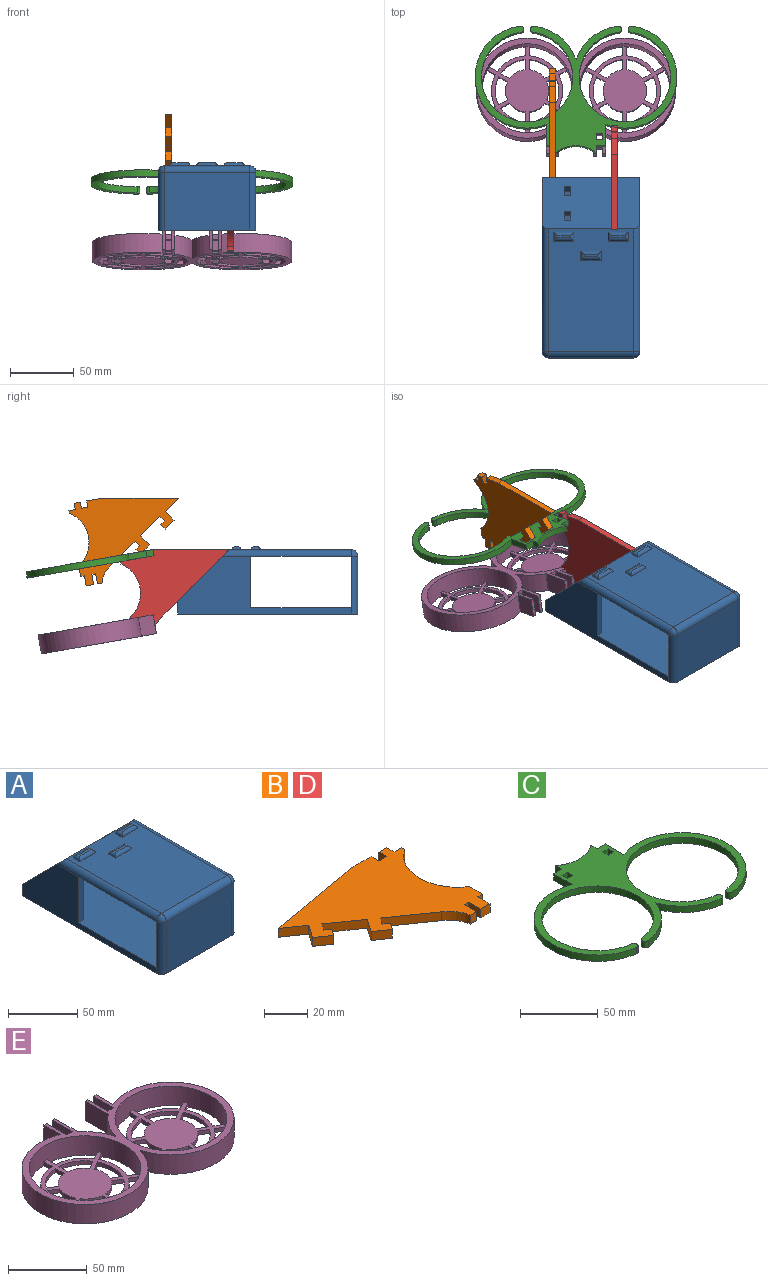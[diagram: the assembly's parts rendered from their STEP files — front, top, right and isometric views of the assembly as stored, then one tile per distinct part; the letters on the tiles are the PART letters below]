
ASSEMBLY  parts=5 mates=10
PART A: 54 faces, bbox 77x142x53 mm
  f0: plane 67x37.57mm, normal (0,-0.71,-0.71), area 3359.9mm2, adj f1,f5,f12,f13,f14,f15,f16,f17
  f1: plane 67x2.93mm, normal (0,-1,0), area 196.2mm2, adj f0,f2,f51,f53
  f2: plane 132x77mm, normal (0,0,1), area 9638.3mm2, adj f1,f4,f10,f11,f50,f51,f52,f53
  f3: plane 96.5x67mm, normal (0,0,1), area 6129.5mm2, adj f7,f31,f32,f33,f34,f35,f36,f37
  f4: plane 77x40.5mm, normal (0,1,0), area 3118.5mm2, adj f2,f5,f43,f46
  f5: plane 94.43x77mm, normal (0,0,-1), area 7121mm2, adj f0,f4,f44,f45,f50,f51,f52,f53
  f6: plane 77x10mm, normal (0,1,0), area 770mm2, adj f7,f9,f10,f11
  f7: plane 77x40.5mm, normal (0,0.71,0.71), area 4195.1mm2, adj f3,f6,f10,f11,f12,f13,f14,f15
  f8: plane 67x45.5mm, normal (0,-1,0), area 3048.5mm2, adj f9,f43,f46,f49
  f9: plane 142x77mm, normal (0,0,-1), area 10923.3mm2, adj f6,f8,f10,f11,f43,f46
  f10: plane 137x45.5mm, normal (1,0,0), area 2386.5mm2, adj f2,f6,f7,f9,f45,f46,f50
  f11: plane 137x45.5mm, normal (-1,0,0), area 2386.5mm2, adj f2,f6,f7,f9,f43,f44,f52
  f12: plane 5x3.54mm, normal (0,-0.71,0.71), area 25mm2, adj f0,f7,f13,f15
  f13: plane 10.61x10.61mm, normal (1,0,0), area 50mm2, adj f0,f7,f12,f14
  f14: plane 5x3.54mm, normal (0,0.71,-0.71), area 25mm2, adj f0,f7,f13,f15
  f15: plane 10.61x10.61mm, normal (-1,0,0), area 50mm2, adj f0,f7,f12,f14
  f16: plane 10.61x10.61mm, normal (1,0,0), area 50mm2, adj f0,f7,f17,f19
  f17: plane 5x3.54mm, normal (0,0.71,-0.71), area 25mm2, adj f0,f7,f16,f18
  f18: plane 10.61x10.61mm, normal (-1,0,0), area 50mm2, adj f0,f7,f17,f19
  f19: plane 5x3.54mm, normal (0,-0.71,0.71), area 25mm2, adj f0,f7,f16,f18
  f20: plane 10.61x10.61mm, normal (1,0,0), area 50mm2, adj f0,f7,f21,f23
  f21: plane 5x3.54mm, normal (0,0.71,-0.71), area 25mm2, adj f0,f7,f20,f22
  f22: plane 10.61x10.61mm, normal (-1,0,0), area 50mm2, adj f0,f7,f21,f23
  f23: plane 5x3.54mm, normal (0,-0.71,0.71), area 25mm2, adj f0,f7,f20,f22
  f24: plane 5x3.54mm, normal (0,-0.71,0.71), area 25mm2, adj f0,f7,f25,f27
  f25: plane 10.61x10.61mm, normal (1,0,0), area 50mm2, adj f0,f7,f24,f26
  f26: plane 5x3.54mm, normal (0,0.71,-0.71), area 25mm2, adj f0,f7,f25,f27
  f27: plane 10.61x10.61mm, normal (-1,0,0), area 50mm2, adj f0,f7,f24,f26
  f28: plane 11x2mm, normal (0,0,1), area 22mm2, adj f39,f40,f41,f42
  f29: plane 11x2mm, normal (0,0,1), area 22mm2, adj f31,f32,f33,f34
  f30: plane 11x2mm, normal (0,0,1), area 22mm2, adj f35,f36,f37,f38
  f31: cylinder r=2.5mm len=7mm, axis (0,-1,0), area 20.4mm2, adj f3,f29,f32,f33
  f32: cylinder r=2.5mm len=16mm, axis (-1,0,0), area 55.7mm2, adj f3,f29,f31,f34
  f33: cylinder r=2.5mm len=16mm, axis (1,0,0), area 55.7mm2, adj f3,f29,f31,f34
  f34: cylinder r=2.5mm len=7mm, axis (0,1,0), area 20.4mm2, adj f3,f29,f32,f33
  f35: cylinder r=2.5mm len=7mm, axis (0,-1,0), area 20.4mm2, adj f3,f30,f36,f37
  f36: cylinder r=2.5mm len=16mm, axis (-1,0,0), area 55.7mm2, adj f3,f30,f35,f38
  f37: cylinder r=2.5mm len=16mm, axis (1,0,0), area 55.7mm2, adj f3,f30,f35,f38
  f38: cylinder r=2.5mm len=7mm, axis (0,1,0), area 20.4mm2, adj f3,f30,f36,f37
  f39: cylinder r=2.5mm len=7mm, axis (0,-1,0), area 20.4mm2, adj f3,f28,f40,f41
  f40: cylinder r=2.5mm len=16mm, axis (-1,0,0), area 55.7mm2, adj f3,f28,f39,f42
  f41: cylinder r=2.5mm len=16mm, axis (1,0,0), area 55.7mm2, adj f3,f28,f39,f42
  f42: cylinder r=2.5mm len=7mm, axis (0,1,0), area 20.4mm2, adj f3,f28,f40,f41
  f43: cylinder r=5mm len=45.5mm, axis (0,0,1), area 357.4mm2, adj f4,f8,f9,f11,f47
  f44: cylinder r=5mm len=101.5mm, axis (0,1,0), area 772.2mm2, adj f3,f5,f7,f11,f47
  f45: cylinder r=5mm len=101.5mm, axis (0,-1,0), area 772.2mm2, adj f3,f5,f7,f10,f48
  f46: cylinder r=5mm len=45.5mm, axis (0,0,-1), area 357.4mm2, adj f4,f8,f9,f10,f48
  f47: sphere r=5mm, area 39.3mm2, adj f43,f44,f49
  f48: sphere r=5mm, area 39.3mm2, adj f45,f46,f49
  f49: cylinder r=5mm len=67mm, axis (1,0,0), area 526.2mm2, adj f3,f8,f47,f48
  f50: plane 40.5x5mm, normal (0,-1,0), area 202.5mm2, adj f2,f5,f10,f51
  f51: plane 52.57x40.5mm, normal (-1,0,0), area 1423.3mm2, adj f0,f1,f2,f5,f50
  f52: plane 40.5x5mm, normal (0,-1,0), area 202.5mm2, adj f2,f5,f11,f53
  f53: plane 52.57x40.5mm, normal (1,0,0), area 1423.3mm2, adj f0,f1,f2,f5,f52
PART B: 35 faces, bbox 86.3x65.7x5 mm
  f0: plane 5x5mm, normal (1,0,0), area 25mm2, adj f1,f32,f33,f34
  f1: plane 13x5mm, normal (0,1,0), area 65mm2, adj f0,f2,f33,f34
  f2: plane 58.34x10.29mm, normal (-0.17,0.98,0), area 296.2mm2, adj f1,f3,f33,f34
  f3: plane 11.88x8.32mm, normal (-0.57,-0.82,0), area 72.5mm2, adj f2,f4,f33,f34
  f4: plane 8.19x5.74mm, normal (-0.82,0.57,0), area 50mm2, adj f3,f5,f33,f34
  f5: plane 8.19x5.74mm, normal (-0.57,-0.82,0), area 50mm2, adj f4,f6,f33,f34
  f6: plane 5x4.15mm, normal (0.82,-0.57,0), area 25.2mm2, adj f5,f7,f33,f34
  f7: plane 5x3.3mm, normal (0.56,0.83,0), area 20mm2, adj f6,f8,f33,f34
  f8: plane 5x4.1mm, normal (0.82,-0.57,0), area 25mm2, adj f7,f9,f33,f34
  f9: plane 17.64x12.35mm, normal (-0.57,-0.82,0), area 107.7mm2, adj f8,f10,f33,f34
  f10: plane 8.19x5.74mm, normal (-0.82,0.57,0), area 50mm2, adj f9,f11,f33,f34
  f11: plane 8.19x5.74mm, normal (-0.57,-0.82,0), area 50mm2, adj f10,f12,f33,f34
  f12: plane 5x4.1mm, normal (0.82,-0.57,0), area 25mm2, adj f11,f13,f33,f34
  f13: plane 5x3.28mm, normal (0.57,0.82,0), area 20mm2, adj f12,f14,f33,f34
  f14: plane 5x4.1mm, normal (0.82,-0.57,0), area 25mm2, adj f13,f15,f33,f34
  f15: plane 23.48x16.44mm, normal (-0.57,-0.82,0), area 143.3mm2, adj f14,f16,f33,f34
  f16: cylinder r=20mm len=8.98mm, axis (0,0,1), area 58.1mm2, adj f15,f17,f33,f34
  f17: plane 5x2.46mm, normal (-0.98,-0.17,0), area 12.5mm2, adj f16,f18,f33,f34
  f18: plane 5x4mm, normal (0,-1,0), area 20mm2, adj f17,f19,f33,f34
  f19: plane 8x5mm, normal (1,0,0), area 40mm2, adj f18,f20,f33,f34
  f20: plane 5x3mm, normal (0,-1,0), area 15mm2, adj f19,f21,f33,f34
  f21: plane 8x5mm, normal (-1,0,0), area 40mm2, adj f20,f22,f33,f34
  f22: plane 6x5mm, normal (0,-1,0), area 30mm2, adj f21,f23,f33,f34
  f23: plane 8x5mm, normal (1,0,0), area 40mm2, adj f22,f24,f33,f34
  f24: plane 5x3mm, normal (0,-1,0), area 15mm2, adj f23,f25,f33,f34
  f25: plane 8.5x5mm, normal (1,0,0), area 42.5mm2, adj f24,f26,f33,f34
  f26: cylinder r=25mm len=42.2mm, axis (0,0,1), area 251.2mm2, adj f25,f27,f33,f34
  f27: plane 5x2mm, normal (1,0,0), area 10mm2, adj f26,f28,f33,f34
  f28: plane 5x5mm, normal (0,1,0), area 25mm2, adj f27,f29,f33,f34
  f29: plane 5x5mm, normal (1,0,0), area 25mm2, adj f28,f30,f33,f34
  f30: plane 5x5mm, normal (0,1,0), area 25mm2, adj f29,f31,f33,f34
  f31: plane 5x5mm, normal (-1,0,0), area 25mm2, adj f30,f32,f33,f34
  f32: plane 5x5mm, normal (0,1,0), area 25mm2, adj f0,f31,f33,f34
  f33: plane 86.34x65.7mm, normal (0,0,1), area 2933.9mm2, adj f0,f1,f2,f3,f4,f5,f6,f7
  f34: plane 86.34x65.7mm, normal (0,0,-1), area 2933.9mm2, adj f0,f1,f2,f3,f4,f5,f6,f7
PART C: 27 faces, bbox 159x101.5x5 mm
  f0: plane 16.84x5mm, normal (1,0,0), area 84.2mm2, adj f1,f24,f25,f26
  f1: plane 7.5x5mm, normal (0,1,0), area 37.5mm2, adj f0,f2,f25,f26
  f2: plane 5.79x5mm, normal (1,0,0), area 29mm2, adj f1,f3,f25,f26
  f3: cylinder r=25mm len=32mm, axis (0,0,1), area 173.6mm2, adj f2,f4,f25,f26
  f4: plane 5.79x5mm, normal (-1,0,0), area 29mm2, adj f3,f5,f25,f26
  f5: plane 7.5x5mm, normal (0,1,0), area 37.5mm2, adj f4,f6,f25,f26
  f6: plane 16.84x5mm, normal (-1,0,0), area 84.2mm2, adj f5,f7,f25,f26
  f7: cylinder r=41mm len=81.65mm, axis (0,0,1), area 694.1mm2, adj f6,f8,f25,f26
  f8: cylinder r=2.5mm len=5mm, axis (0,0,1), area 39.3mm2, adj f7,f9,f25,f26
  f9: cylinder r=36mm len=72mm, axis (0,0,1), area 1084.1mm2, adj f8,f10,f25,f26
  f10: cylinder r=2.5mm len=5mm, axis (0,0,1), area 39.3mm2, adj f9,f11,f25,f26
  f11: cylinder r=41mm len=33.18mm, axis (0,0,1), area 223.4mm2, adj f10,f12,f25,f26
  f12: cylinder r=41mm len=33.18mm, axis (0,0,1), area 223.4mm2, adj f11,f13,f25,f26
  f13: cylinder r=2.5mm len=5mm, axis (0,0,1), area 39.3mm2, adj f12,f14,f25,f26
  f14: cylinder r=36mm len=72mm, axis (0,0,1), area 1084.1mm2, adj f13,f15,f25,f26
  f15: cylinder r=2.5mm len=5mm, axis (0,0,1), area 39.3mm2, adj f14,f24,f25,f26
  f16: plane 5x5mm, normal (-1,0,0), area 25mm2, adj f17,f23,f25,f26
  f17: plane 5x5mm, normal (0,1,0), area 25mm2, adj f16,f18,f25,f26
  f18: plane 5x5mm, normal (1,0,0), area 25mm2, adj f17,f23,f25,f26
  f19: plane 5x5mm, normal (-1,0,0), area 25mm2, adj f20,f22,f25,f26
  f20: plane 5x5mm, normal (0,1,0), area 25mm2, adj f19,f21,f25,f26
  f21: plane 5x5mm, normal (1,0,0), area 25mm2, adj f20,f22,f25,f26
  f22: plane 5x5mm, normal (0,-1,0), area 25mm2, adj f19,f21,f25,f26
  f23: plane 5x5mm, normal (0,-1,0), area 25mm2, adj f16,f18,f25,f26
  f24: cylinder r=41mm len=81.65mm, axis (0,0,1), area 694.1mm2, adj f0,f15,f25,f26
  f25: plane 159x101.46mm, normal (0,0,1), area 3465.8mm2, adj f0,f1,f2,f3,f4,f5,f6,f7
  f26: plane 159x101.46mm, normal (0,0,-1), area 3465.8mm2, adj f0,f1,f2,f3,f4,f5,f6,f7
PART D: same geometry as B
PART E: 122 faces, bbox 157x92x15 mm
  f0: plane 5x3mm, normal (0,1,0), area 15mm2, adj f1,f35,f108,f121
  f1: plane 18x15mm, normal (1,0,0), area 230.3mm2, adj f0,f36,f37,f108,f109,f110,f111,f112
  f2: plane 5x3mm, normal (0,1,0), area 15mm2, adj f3,f98,f108,f118
  f3: plane 18x15mm, normal (1,0,0), area 230.3mm2, adj f2,f28,f29,f108,f109,f113,f114,f115
  f4: plane 71x62.93mm, normal (0,0,1), area 1686.6mm2, adj f19,f20,f21,f22,f23,f24,f25,f43
  f5: plane 71x62.93mm, normal (0,0,1), area 1686.6mm2, adj f6,f7,f8,f9,f10,f11,f12,f13
  f6: cylinder r=25mm len=19.36mm, axis (0,0,1), area 69.5mm2, adj f5,f7,f107,f108
  f7: plane 8.02x3mm, normal (-1,0,0), area 24.1mm2, adj f5,f6,f8,f108
  f8: cylinder r=17mm len=12.42mm, axis (0,0,1), area 44.4mm2, adj f5,f7,f107,f108
  f9: plane 7.51x3mm, normal (-1,0,0), area 22.5mm2, adj f5,f86,f106,f108
  f10: plane 6.5x3.75mm, normal (0.5,-0.87,0), area 22.5mm2, adj f5,f86,f106,f108
  f11: plane 8.02x3mm, normal (1,0,0), area 24.1mm2, adj f5,f12,f105,f108
  f12: cylinder r=25mm len=19.36mm, axis (0,0,1), area 69.5mm2, adj f5,f11,f13,f108
  f13: plane 6.95x4.01mm, normal (-0.5,0.87,0), area 24.1mm2, adj f5,f12,f105,f108
  f14: plane 6.5x3.75mm, normal (-0.5,-0.87,0), area 22.5mm2, adj f5,f86,f104,f108
  f15: plane 7.51x3mm, normal (1,0,0), area 22.5mm2, adj f5,f86,f104,f108
  f16: cylinder r=25mm len=22.36mm, axis (0,0,1), area 69.5mm2, adj f5,f17,f103,f108
  f17: plane 6.95x4.01mm, normal (0.5,0.87,0), area 24.1mm2, adj f5,f16,f18,f108
  f18: cylinder r=17mm len=14.34mm, axis (0,0,1), area 44.4mm2, adj f5,f17,f103,f108
  f19: plane 6.5x3.75mm, normal (-0.5,-0.87,0), area 22.5mm2, adj f4,f20,f94,f108
  f20: cylinder r=28mm len=25.36mm, axis (0,0,1), area 79mm2, adj f4,f19,f102,f108
  f21: plane 6.95x4.01mm, normal (-0.5,-0.87,0), area 24.1mm2, adj f4,f22,f101,f108
  f22: cylinder r=25mm len=19.36mm, axis (0,0,1), area 69.5mm2, adj f4,f21,f23,f108
  f23: plane 8.02x3mm, normal (1,0,0), area 24.1mm2, adj f4,f22,f101,f108
  f24: plane 6.5x3.75mm, normal (0.5,-0.87,0), area 22.5mm2, adj f4,f94,f100,f108
  f25: plane 6.5x3.75mm, normal (0.5,0.87,0), area 22.5mm2, adj f4,f94,f100,f108
  f26: plane 6.5x3.75mm, normal (0.5,-0.87,0), area 22.5mm2, adj f5,f86,f99,f108
  f27: plane 6.5x3.75mm, normal (0.5,0.87,0), area 22.5mm2, adj f5,f86,f99,f108
  f28: plane 5x4mm, normal (0,1,0), area 20mm2, adj f3,f98,f109,f117
  f29: plane 15x2.5mm, normal (0,1,0), area 37.5mm2, adj f3,f30,f108,f109
  f30: plane 20.78x15mm, normal (-1,0,0), area 311.6mm2, adj f29,f31,f108,f109
  f31: cylinder r=40mm len=20.37mm, axis (0,0,1), area 372.6mm2, adj f30,f32,f108,f109
  f32: cylinder r=40mm len=20.37mm, axis (0,0,1), area 372.6mm2, adj f31,f33,f108,f109
  f33: plane 20.78x15mm, normal (1,0,0), area 311.6mm2, adj f32,f34,f108,f109
  f34: plane 15x2.5mm, normal (0,1,0), area 37.5mm2, adj f33,f35,f108,f109
  f35: plane 18x15mm, normal (-1,0,0), area 230.3mm2, adj f0,f34,f36,f108,f109,f110,f111,f112
  f36: plane 5x4mm, normal (0,1,0), area 20mm2, adj f1,f35,f109,f120
  f37: plane 15x2.5mm, normal (0,1,0), area 37.5mm2, adj f1,f38,f108,f109
  f38: plane 15x14.92mm, normal (-1,0,0), area 223.8mm2, adj f37,f39,f108,f109
  f39: cylinder r=40mm len=80mm, axis (0,0,1), area 2893.2mm2, adj f38,f40,f108,f109
  f40: cylinder r=40mm len=80mm, axis (0,0,1), area 2893.2mm2, adj f39,f41,f108,f109
  f41: plane 15x14.92mm, normal (1,0,0), area 223.8mm2, adj f40,f42,f108,f109
  f42: plane 15x2.5mm, normal (0,1,0), area 37.5mm2, adj f41,f98,f108,f109
  f43: plane 6.95x4.01mm, normal (0.5,0.87,0), area 24.1mm2, adj f4,f44,f97,f108
  f44: cylinder r=17mm len=14.34mm, axis (0,0,1), area 44.4mm2, adj f4,f43,f45,f108
  f45: plane 6.95x4.01mm, normal (0.5,-0.87,0), area 24.1mm2, adj f4,f44,f97,f108
  f46: cylinder r=17mm len=14.34mm, axis (0,0,1), area 44.4mm2, adj f4,f47,f96,f108
  f47: plane 6.95x4.01mm, normal (-0.5,0.87,0), area 24.1mm2, adj f4,f46,f48,f108
  f48: cylinder r=25mm len=22.36mm, axis (0,0,1), area 69.5mm2, adj f4,f47,f96,f108
  f49: plane 6.5x3.75mm, normal (0.5,0.87,0), area 22.5mm2, adj f4,f94,f95,f108
  f50: plane 7.51x3mm, normal (-1,0,0), area 22.5mm2, adj f4,f94,f95,f108
  f51: plane 6.5x3.75mm, normal (0.5,-0.87,0), area 22.5mm2, adj f4,f52,f94,f108
  f52: cylinder r=28mm len=21.96mm, axis (0,0,1), area 79mm2, adj f4,f51,f53,f108
  f53: plane 7.51x3mm, normal (-1,0,0), area 22.5mm2, adj f4,f52,f94,f108
  f54: plane 6.95x4.01mm, normal (0.5,-0.87,0), area 24.1mm2, adj f4,f55,f93,f108
  f55: cylinder r=17mm len=12.42mm, axis (0,0,1), area 44.4mm2, adj f4,f54,f56,f108
  f56: plane 8.02x3mm, normal (-1,0,0), area 24.1mm2, adj f4,f55,f93,f108
  f57: cylinder r=17mm len=12.42mm, axis (0,0,1), area 44.4mm2, adj f4,f58,f92,f108
  f58: plane 6.95x4.01mm, normal (0.5,0.87,0), area 24.1mm2, adj f4,f57,f59,f108
  f59: cylinder r=25mm len=19.36mm, axis (0,0,1), area 69.5mm2, adj f4,f58,f92,f108
  f60: plane 6.95x4.01mm, normal (-0.5,0.87,0), area 24.1mm2, adj f4,f61,f91,f108
  f61: cylinder r=17mm len=12.42mm, axis (0,0,1), area 44.4mm2, adj f4,f60,f62,f108
  f62: plane 8.02x3mm, normal (1,0,0), area 24.1mm2, adj f4,f61,f91,f108
  f63: cylinder r=28mm len=21.96mm, axis (0,0,1), area 79mm2, adj f4,f64,f90,f108
  f64: plane 7.51x3mm, normal (1,0,0), area 22.5mm2, adj f4,f63,f94,f108
  f65: plane 6.5x3.75mm, normal (-0.5,-0.87,0), area 22.5mm2, adj f4,f89,f94,f108
  f66: plane 7.51x3mm, normal (1,0,0), area 22.5mm2, adj f4,f89,f94,f108
  f67: plane 6.95x4.01mm, normal (-0.5,-0.87,0), area 24.1mm2, adj f5,f68,f88,f108
  f68: cylinder r=25mm len=19.36mm, axis (0,0,1), area 69.5mm2, adj f5,f67,f69,f108
  f69: plane 8.02x3mm, normal (1,0,0), area 24.1mm2, adj f5,f68,f88,f108
  f70: cylinder r=28mm len=25.36mm, axis (0,0,1), area 79mm2, adj f5,f71,f87,f108
  f71: plane 6.5x3.75mm, normal (-0.5,0.87,0), area 22.5mm2, adj f5,f70,f86,f108
  f72: plane 6.5x3.75mm, normal (-0.5,0.87,0), area 22.5mm2, adj f5,f73,f86,f108
  f73: cylinder r=28mm len=21.96mm, axis (0,0,1), area 79mm2, adj f5,f72,f74,f108
  f74: plane 7.51x3mm, normal (1,0,0), area 22.5mm2, adj f5,f73,f86,f108
  f75: plane 6.5x3.75mm, normal (0.5,0.87,0), area 22.5mm2, adj f5,f85,f86,f108
  f76: plane 7.51x3mm, normal (-1,0,0), area 22.5mm2, adj f5,f85,f86,f108
  f77: plane 8.02x3mm, normal (-1,0,0), area 24.1mm2, adj f5,f78,f84,f108
  f78: cylinder r=25mm len=19.36mm, axis (0,0,1), area 69.5mm2, adj f5,f77,f79,f108
  f79: plane 6.95x4.01mm, normal (0.5,-0.87,0), area 24.1mm2, adj f5,f78,f84,f108
  f80: plane 6.95x4.01mm, normal (-0.5,0.87,0), area 24.1mm2, adj f5,f81,f83,f108
  f81: cylinder r=25mm len=22.36mm, axis (0,0,1), area 69.5mm2, adj f5,f80,f82,f108
  f82: plane 6.95x4.01mm, normal (-0.5,-0.87,0), area 24.1mm2, adj f5,f81,f83,f108
  f83: cylinder r=17mm len=14.34mm, axis (0,0,1), area 44.4mm2, adj f5,f80,f82,f108
  f84: cylinder r=17mm len=12.42mm, axis (0,0,1), area 44.4mm2, adj f5,f77,f79,f108
  f85: cylinder r=28mm len=21.96mm, axis (0,0,1), area 79mm2, adj f5,f75,f76,f108
  f86: cylinder r=35.5mm len=71mm, axis (0,0,1), area 3291.8mm2, adj f5,f9,f10,f14,f15,f26,f27,f71
  f87: plane 6.5x3.75mm, normal (-0.5,-0.87,0), area 22.5mm2, adj f5,f70,f86,f108
  f88: cylinder r=17mm len=12.42mm, axis (0,0,1), area 44.4mm2, adj f5,f67,f69,f108
  f89: cylinder r=28mm len=21.96mm, axis (0,0,1), area 79mm2, adj f4,f65,f66,f108
  f90: plane 6.5x3.75mm, normal (-0.5,0.87,0), area 22.5mm2, adj f4,f63,f94,f108
  f91: cylinder r=25mm len=19.36mm, axis (0,0,1), area 69.5mm2, adj f4,f60,f62,f108
  f92: plane 8.02x3mm, normal (-1,0,0), area 24.1mm2, adj f4,f57,f59,f108
  f93: cylinder r=25mm len=19.36mm, axis (0,0,1), area 69.5mm2, adj f4,f54,f56,f108
  f94: cylinder r=35.5mm len=71mm, axis (0,0,1), area 3291.8mm2, adj f4,f19,f24,f25,f49,f50,f51,f53
  f95: cylinder r=28mm len=21.96mm, axis (0,0,1), area 79mm2, adj f4,f49,f50,f108
  f96: plane 6.95x4.01mm, normal (-0.5,-0.87,0), area 24.1mm2, adj f4,f46,f48,f108
  f97: cylinder r=25mm len=22.36mm, axis (0,0,1), area 69.5mm2, adj f4,f43,f45,f108
  f98: plane 18x15mm, normal (-1,0,0), area 230.3mm2, adj f2,f28,f42,f108,f109,f113,f114,f115
  f99: cylinder r=28mm len=25.36mm, axis (0,0,1), area 79mm2, adj f5,f26,f27,f108
  f100: cylinder r=28mm len=25.36mm, axis (0,0,1), area 79mm2, adj f4,f24,f25,f108
  f101: cylinder r=17mm len=12.42mm, axis (0,0,1), area 44.4mm2, adj f4,f21,f23,f108
  f102: plane 6.5x3.75mm, normal (-0.5,0.87,0), area 22.5mm2, adj f4,f20,f94,f108
  f103: plane 6.95x4.01mm, normal (0.5,-0.87,0), area 24.1mm2, adj f5,f16,f18,f108
  f104: cylinder r=28mm len=21.96mm, axis (0,0,1), area 79mm2, adj f5,f14,f15,f108
  f105: cylinder r=17mm len=12.42mm, axis (0,0,1), area 44.4mm2, adj f5,f11,f13,f108
  f106: cylinder r=28mm len=21.96mm, axis (0,0,1), area 79mm2, adj f5,f9,f10,f108
  f107: plane 6.95x4.01mm, normal (0.5,0.87,0), area 24.1mm2, adj f5,f6,f8,f108
  f108: plane 157x92mm, normal (0,0,-1), area 5664.8mm2, adj f0,f1,f2,f3,f6,f7,f8,f9
  f109: plane 157x92mm, normal (0,0,1), area 2261.6mm2, adj f1,f3,f28,f29,f30,f31,f32,f33
  f110: plane 8x5mm, normal (0,-1,0), area 40mm2, adj f1,f35,f108,f112
  f111: plane 8x5mm, normal (0,1,0), area 40mm2, adj f1,f35,f108,f112
  f112: plane 5x3mm, normal (0,0,1), area 15mm2, adj f1,f35,f110,f111
  f113: plane 8x5mm, normal (0,1,0), area 40mm2, adj f3,f98,f108,f115
  f114: plane 8x5mm, normal (0,-1,0), area 40mm2, adj f3,f98,f108,f115
  f115: plane 5x3mm, normal (0,0,1), area 15mm2, adj f3,f98,f113,f114
  f116: plane 8x5mm, normal (0,1,0), area 40mm2, adj f3,f98,f117,f118
  f117: plane 5x1.97mm, normal (0,0,1), area 9.8mm2, adj f3,f28,f98,f116
  f118: plane 5x1.97mm, normal (0,0,-1), area 9.8mm2, adj f2,f3,f98,f116
  f119: plane 8x5mm, normal (0,1,0), area 40mm2, adj f1,f35,f120,f121
  f120: plane 5x1.97mm, normal (0,0,1), area 9.8mm2, adj f1,f35,f36,f119
  f121: plane 5x1.97mm, normal (0,0,-1), area 9.8mm2, adj f0,f1,f35,f119
PLACE A t=(-38.5,-71.5,25.25)mm
PLACE B rot(axis=(0.54,0.64,0.54),114.4deg) t=(-71.32,94.73,56.38)mm
PLACE C rot(axis=(0,-0.09,-1),180deg) t=(-50.32,78.42,35.32)mm
PLACE D rot(axis=(0.54,0.64,0.54),114.4deg) t=(-22.5,54.13,16.15)mm
PLACE E rot(axis=(0,-0.09,-1),180deg) t=(-50.32,67.88,-24.46)mm
MATE planar B.f8 <-> A.f12  axis (0,0.71,-0.71) through (-68.82,12.29,75)mm
MATE planar C.f2 <-> B.f33  axis (-1,0,0) through (-66.32,21.84,47.84)mm
MATE planar A.f7 <-> D.f9  axis (0,0.71,0.71) through (-38.5,-20.18,30.18)mm
MATE planar C.f26 <-> D.f32  axis (0,-0.17,-0.98) through (-31.82,29.18,44)mm
MATE cylindrical C.f14 <-> E.f86  axis (0,0.17,0.98) through (-88.82,78.85,37.78)mm
MATE planar D.f20 <-> E.f115  axis (0,-0.17,-0.98) through (-20,25.45,-8.85)mm
MATE planar E.f98 <-> B.f34  axis (1,0,0) through (-71.32,26.92,-9.11)mm
MATE planar D.f14 <-> A.f23  axis (0,0.71,-0.71) through (-20,-8.84,15.3)mm
MATE planar D.f33 <-> A.f27  axis (1,0,0) through (-17.5,7.15,26.43)mm
MATE planar D.f21 <-> E.f110  axis (0,-0.98,0.17) through (-20,25.53,-16.99)mm
